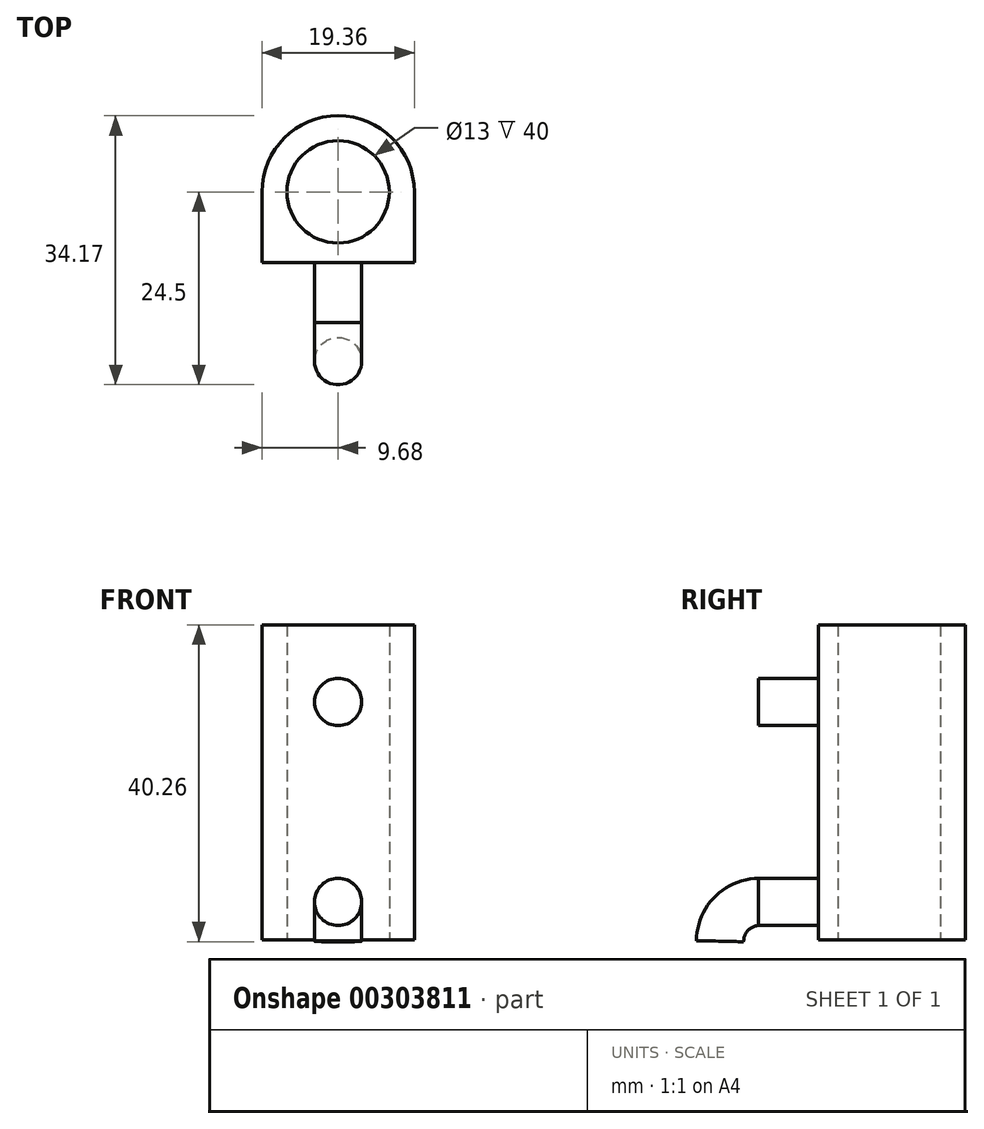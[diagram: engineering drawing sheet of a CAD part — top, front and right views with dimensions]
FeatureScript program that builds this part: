
annotation { "Feature Type Name" : "Feature", "Feature Type Description" : "" }
export const myFeature = defineFeature(function(context is Context, id is Id, definition is map)
    precondition{}
    {
        {
            var Q0;
            Q0=qCreatedBy(makeId("Front.planeOp"),FACE);
            var sketch = newSketch(context, id + "F0", { "sketchPlane" : qUnion([Q0])});
            skLineSegment(sketch, "E0.bottom", {"start": v(0, 0) * mm, "end": v(20, 0) * mm});
            skLineSegment(sketch, "E0.top", {"start": v(0, -40) * mm, "end": v(20, -40) * mm});
            skLineSegment(sketch, "E0.left", {"start": v(0, 0) * mm, "end": v(0, -40) * mm});
            skLineSegment(sketch, "E0.right", {"start": v(20, 0) * mm, "end": v(20, -40) * mm});
            skLineSegment(sketch, "E1", {"start": v(10, -34.5) * mm, "end": v(10, -35.2) * mm});
            skPoint(sketch, "E2", {"position": v(10, -9.8) * mm});
            skCircle(sketch, "E3", {"center": v(10, -9.8) * mm, "radius": 3.18 * mm});
            skCircle(sketch, "E4", {"center": v(10, -35.2) * mm, "radius": 3.18 * mm});
            skSolve(sketch);
        }
        {
            var Q0;
            Q0=makeQuery(id+"F0.imprint","IMPRINT",FACE,{"disambiguationData":[TD([[makeQuery(id+"F0.imprint","IMPRINT",EDGE,{"derivedFrom":sQuery(id+"F0.wireOp",EDGE,"E0.bottom")}),-1.0]])]});
            var Q1;
            Q1=makeQuery(id+"F0.imprint","IMPRINT",FACE,{"disambiguationData":[TD([[makeQuery(id+"F0.imprint","IMPRINT",EDGE,{"derivedFrom":sQuery(id+"F0.wireOp",EDGE,"lxQxVZ59-8Nj6-a4hZ-NJuI-hvmCPkOdnCKT")}),1.0]])]});
            var Q2;
            Q2=makeQuery(id+"F0.imprint","IMPRINT",FACE,{"disambiguationData":[TD([[makeQuery(id+"F0.imprint","IMPRINT",EDGE,{"derivedFrom":sQuery(id+"F0.wireOp",EDGE,"DWrYotNM-sBmh-saPB-KEn7-38WvWVFyXRDX")}),1.0]])]});
            var Q3;
            Q3=makeQuery(id+"FpAVMRyOPs3kxoD_0.opExtrude","CAP_FACE",FACE,{"disambiguationData":[OSD([sQuery(id+"F0.wireOp",EDGE,"E3")])],"isStart":false});
            var Q4;
            Q4=makeQuery(id+"F0.imprint","IMPRINT",FACE,{"disambiguationData":[TD([[makeQuery(id+"F0.imprint","IMPRINT",EDGE,{"derivedFrom":sQuery(id+"F0.wireOp",EDGE,"E4")}),1.0]])]});
            var Q5;
            Q5=makeQuery(id+"F0.imprint","IMPRINT",FACE,{"disambiguationData":[TD([[makeQuery(id+"F0.imprint","IMPRINT",EDGE,{"derivedFrom":sQuery(id+"F0.wireOp",EDGE,"E3")}),1.0]])]});
            extrude(context, id + "F1", {"entities" : qUnion([Q0, Q1, Q2, Q3, Q4, Q5]), "oppositeDirection" : true, "depth" : 19 * mm});
        }
        {
            var Q0;
            Q0=makeQuery(id+"F1.opExtrude","SWEPT_FACE",FACE,{"disambiguationData":[OSD([sQuery(id+"F0.wireOp",EDGE,"E0.top")])]});
            var sketch = newSketch(context, id + "F2", { "sketchPlane" : qUnion([Q0])});
            skPoint(sketch, "E5", {"position": v(10, -9) * mm});
            skCircle(sketch, "E6", {"center": v(10, -9) * mm, "radius": 6.5 * mm});
            skArc(sketch, "E7.0", {"start": v(0.32, -9) * mm, "mid": v(10, -18.68) * mm, "end": v(19.67, -9) * mm});
            skLineSegment(sketch, "E8", {"start": v(0.32, -9) * mm, "end": v(0.32, 0) * mm});
            skLineSegment(sketch, "E9", {"start": v(19.67, -9) * mm, "end": v(19.67, 0) * mm});
            skLineSegment(sketch, "E10", {"start": v(0.32, 0) * mm, "end": v(19.67, 0) * mm});
            skSolve(sketch);
        }
        {
            var Q0;
            Q0=makeQuery(id+"F1.opExtrude","CAP_FACE",FACE,{"disambiguationData":[OSD([sQuery(id+"F0.wireOp",EDGE,"E0.bottom"),sQuery(id+"F0.wireOp",EDGE,"E0.top"),sQuery(id+"F0.wireOp",EDGE,"E0.left"),sQuery(id+"F0.wireOp",EDGE,"E0.right")])],"isStart":true});
            var sketch = newSketch(context, id + "F3", { "sketchPlane" : qUnion([Q0])});
            skPoint(sketch, "E11", {"position": v(10, -35.2) * mm});
            skPoint(sketch, "E12", {"position": v(10, -9.8) * mm});
            skCircle(sketch, "E13", {"center": v(10, -35.2) * mm, "radius": 3 * mm});
            skCircle(sketch, "E14", {"center": v(10, -9.8) * mm, "radius": 3 * mm});
            skSolve(sketch);
        }
        {
            var Q0;
            Q0=makeQuery(id+"F3.imprint","IMPRINT",FACE,{"disambiguationData":[TD([[makeQuery(id+"F3.imprint","IMPRINT",EDGE,{"derivedFrom":sQuery(id+"F3.wireOp",EDGE,"E13")}),1.0]])]});
            var Q1;
            Q1=makeQuery(id+"F3.imprint","IMPRINT",FACE,{"disambiguationData":[TD([[makeQuery(id+"F3.imprint","IMPRINT",EDGE,{"derivedFrom":sQuery(id+"F3.wireOp",EDGE,"E14")}),1.0]])]});
            extrude(context, id + "F4", {"entities" : qUnion([Q0, Q1]), "operationType" : NewBodyOperationType.ADD, "depth" : 7.62 * mm, "offsetDistance" : 25.4 * mm});
        }
        {
            var Q0;
            Q0=makeQuery(id+"F2.imprint","IMPRINT",FACE,{"disambiguationData":[TD([[makeQuery(id+"F2.imprint","IMPRINT",EDGE,{"derivedFrom":sQuery(id+"F2.wireOp",EDGE,"E7.0")}),-1.0]])]});
            var Q1;
            Q1=makeQuery(id+"F2.imprint","IMPRINT",FACE,{"disambiguationData":[TD([[makeQuery(id+"F2.imprint","IMPRINT",EDGE,{"derivedFrom":sQuery(id+"F2.wireOp",EDGE,"E6")}),1.0]])]});
            extrude(context, id + "F5", {"entities" : qUnion([Q0, Q1]), "operationType" : NewBodyOperationType.REMOVE, "endBound" : BoundingType.THROUGH_ALL, "oppositeDirection" : true, "depth" : 25.4 * mm, "offsetDistance" : 25.4 * mm});
        }
        {
            var Q0;
            Q0=makeQuery(id+"F4.opExtrude","CAP_FACE",FACE,{"disambiguationData":[OSD([sQuery(id+"F3.wireOp",EDGE,"E13")])],"isStart":false});
            var sketch = newSketch(context, id + "F6", { "sketchPlane" : qUnion([Q0])});
            skCircle(sketch, "E15.0", {"center": v(10, -35.2) * mm, "radius": 3 * mm});
            skLineSegment(sketch, "E16", {"start": v(10, -32.2) * mm, "end": v(10, -38.2) * mm});
            skSolve(sketch);
        }
        {
            var Q0;
            Q0=sQuery(id+"F6.wireOp",EDGE,"E16");
            cPlane(context, id + "F7", {"entities" : qUnion([Q0]), "cplaneType" : CPlaneType.LINE_ANGLE, "offset" : 25 * mm, "angle" : 0 * degree, "width" : 150 * mm, "height" : 150 * mm});
        }
        {
            var Q0;
            Q0=qCreatedBy(id+"F7.planeOp",FACE);
            var sketch = newSketch(context, id + "F8", { "sketchPlane" : qUnion([Q0])});
            skPoint(sketch, "E17.0", {"position": v(7.62, -35.2) * mm});
            skLineSegment(sketch, "E18", {"start": v(7.62, -35.2) * mm, "end": v(7.5, -40.2) * mm});
            skArc(sketch, "E19", {"start": v(7.62, -35.2) * mm, "mid": v(11.08, -36.7) * mm, "end": v(12.5, -40.2) * mm});
            skSolve(sketch);
        }
        {
            var Q0;
            {var subQ0=sQuery(id+"F6.wireOp",EDGE,"E16");Q0=makeQuery(id+"F6.imprint","IMPRINT",FACE,{"disambiguationData":[TD([[makeQuery(id+"F6.imprint","IMPRINT",EDGE,{"derivedFrom":subQ0}),1.0]])]});}
            var Q1;
            {var subQ0=sQuery(id+"F6.wireOp",EDGE,"E16");Q1=makeQuery(id+"F6.imprint","IMPRINT",FACE,{"disambiguationData":[TD([[makeQuery(id+"F6.imprint","IMPRINT",EDGE,{"derivedFrom":subQ0}),-1.0]])]});}
            var Q2;
            Q2=sQuery(id+"F8.wireOp",EDGE,"E19");
            sweep(context, id + "F9", {"operationType" : NewBodyOperationType.ADD, "profiles" : qUnion([Q0, Q1]), "path" : qUnion([Q2])});
        }
    });
